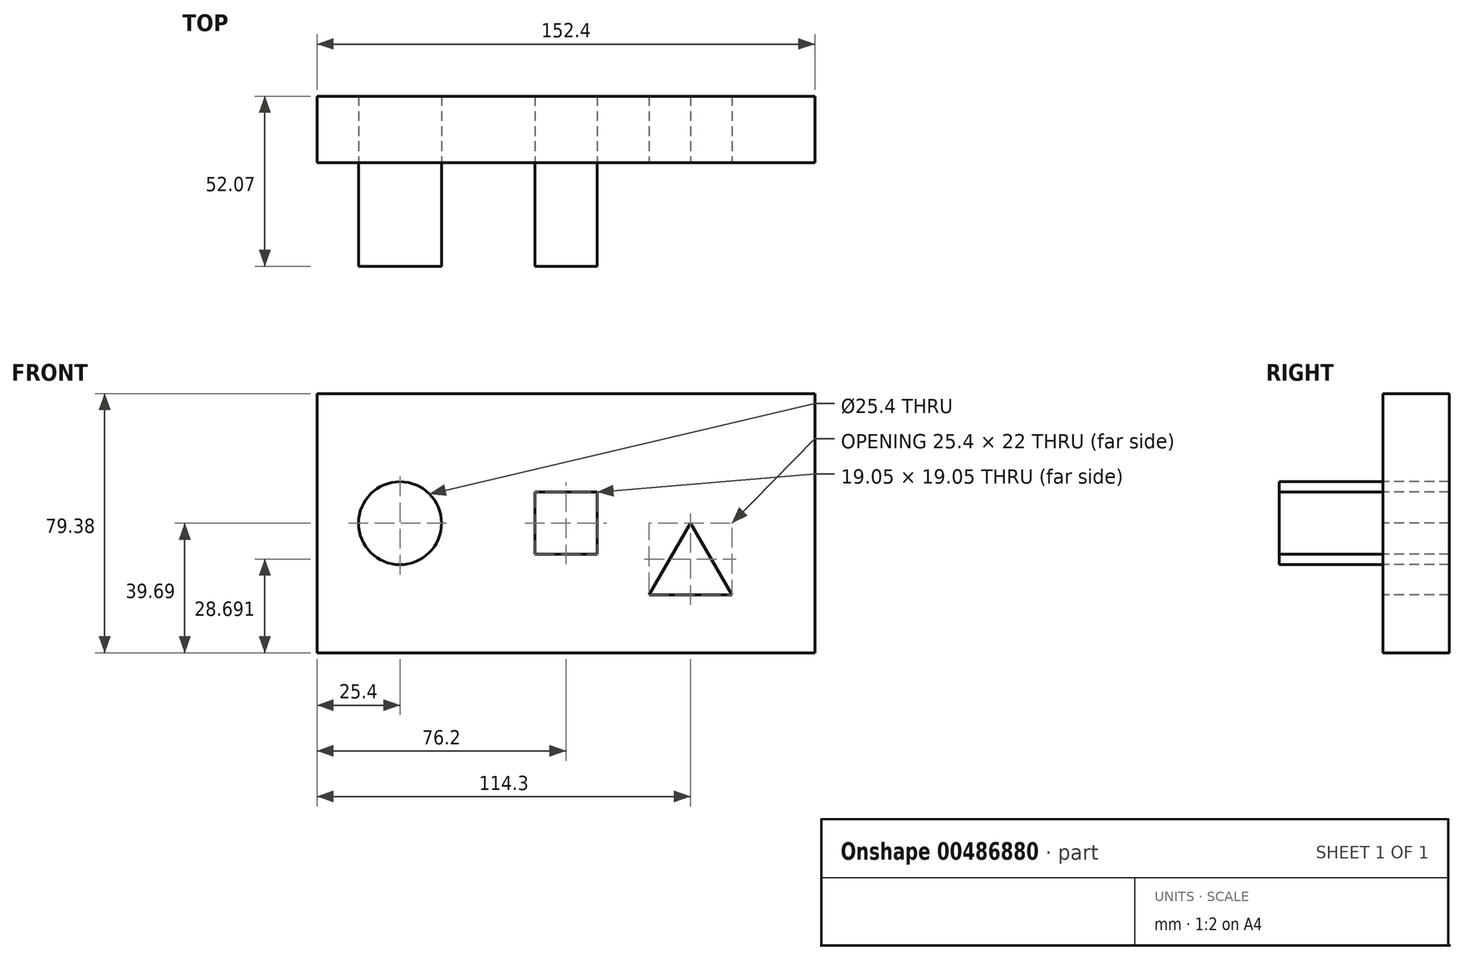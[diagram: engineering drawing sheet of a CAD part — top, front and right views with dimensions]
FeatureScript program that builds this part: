
annotation { "Feature Type Name" : "Feature", "Feature Type Description" : "" }
export const myFeature = defineFeature(function(context is Context, id is Id, definition is map)
    precondition{}
    {
        {
            var Q0;
            Q0=qCreatedBy(makeId("Front.planeOp"),FACE);
            var sketch = newSketch(context, id + "F0", { "sketchPlane" : qUnion([Q0])});
            skLineSegment(sketch, "E0", {"start": v(6.35, 0) * mm, "end": v(-6.35, -22) * mm});
            skLineSegment(sketch, "E1", {"start": v(-6.35, -22) * mm, "end": v(19.05, -22) * mm});
            skLineSegment(sketch, "E2", {"start": v(19.05, -22) * mm, "end": v(6.35, 0) * mm});
            skLineSegment(sketch, "E3.bottom", {"start": v(-22.23, -9.53) * mm, "end": v(-41.28, -9.52) * mm});
            skLineSegment(sketch, "E3.top", {"start": v(-22.23, 9.53) * mm, "end": v(-41.28, 9.53) * mm});
            skLineSegment(sketch, "E3.left", {"start": v(-22.23, -9.53) * mm, "end": v(-22.23, 9.53) * mm});
            skLineSegment(sketch, "E3.right", {"start": v(-41.28, -9.52) * mm, "end": v(-41.28, 9.53) * mm});
            skPoint(sketch, "E3.middle", {"position": v(-31.75, 0) * mm});
            skCircle(sketch, "E4", {"center": v(-82.55, 0) * mm, "radius": 12.7 * mm});
            skPoint(sketch, "E5.middle", {"position": v(0, 0) * mm});
            skLineSegment(sketch, "E6.bottom", {"start": v(-107.95, -39.69) * mm, "end": v(44.45, -39.69) * mm});
            skLineSegment(sketch, "E6.top", {"start": v(-107.95, 39.69) * mm, "end": v(44.45, 39.69) * mm});
            skLineSegment(sketch, "E6.left", {"start": v(-107.95, -39.69) * mm, "end": v(-107.95, 39.69) * mm});
            skLineSegment(sketch, "E6.right", {"start": v(44.45, -39.69) * mm, "end": v(44.45, 39.69) * mm});
            skSolve(sketch);
        }
        {
            var Q0;
            Q0=makeQuery(id+"F0.imprint","IMPRINT",FACE,{"disambiguationData":[TD([[makeQuery(id+"F0.imprint","IMPRINT",EDGE,{"derivedFrom":sQuery(id+"F0.wireOp",EDGE,"E0")}),-1.0]])]});
            extrude(context, id + "F1", {"entities" : qUnion([Q0]), "oppositeDirection" : true, "depth" : 20.32 * mm});
        }
        {
            var Q0;
            Q0=makeQuery(id+"F0.imprint","IMPRINT",FACE,{"disambiguationData":[TD([[makeQuery(id+"F0.imprint","IMPRINT",EDGE,{"derivedFrom":sQuery(id+"F0.wireOp",EDGE,"E4")}),1.0]])]});
            extrude(context, id + "F2", {"entities" : qUnion([Q0]), "oppositeDirection" : true, "depth" : 20.32 * mm, "hasSecondDirection" : true, "secondDirectionOppositeDirection" : false, "secondDirectionDepth" : 31.75 * mm});
        }
        {
            var Q0;
            Q0=makeQuery(id+"F0.imprint","IMPRINT",FACE,{"disambiguationData":[TD([[makeQuery(id+"F0.imprint","IMPRINT",EDGE,{"derivedFrom":sQuery(id+"F0.wireOp",EDGE,"E3.bottom")}),-1.0]])]});
            extrude(context, id + "F3", {"entities" : qUnion([Q0]), "depth" : 31.75 * mm});
        }
    });
